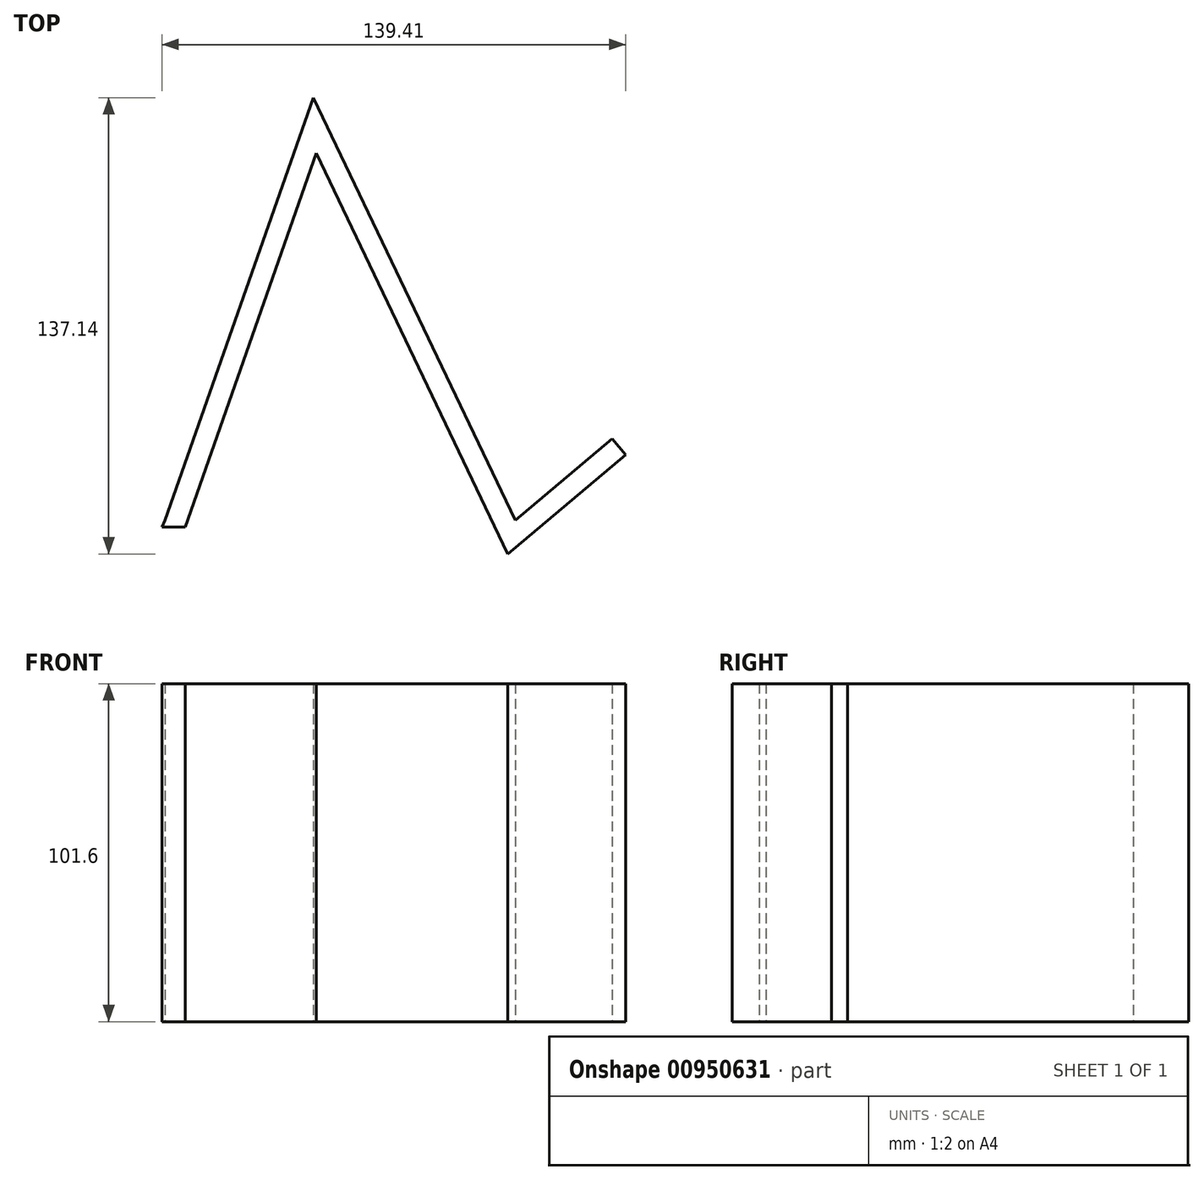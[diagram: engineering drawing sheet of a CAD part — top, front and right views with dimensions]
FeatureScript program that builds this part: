
annotation { "Feature Type Name" : "Feature", "Feature Type Description" : "" }
export const myFeature = defineFeature(function(context is Context, id is Id, definition is map)
    precondition{}
    {
        {
            var Q0;
            Q0=qCreatedBy(makeId("Top.planeOp"),FACE);
            var sketch = newSketch(context, id + "F0", { "sketchPlane" : qUnion([Q0])});
            skLineSegment(sketch, "E0", {"start": v(0, 0) * mm, "end": v(-60.67, 127) * mm});
            skLineSegment(sketch, "E1", {"start": v(-60.67, 127) * mm, "end": v(-105.18, 0) * mm});
            skLineSegment(sketch, "E2", {"start": v(0, 0) * mm, "end": v(29.17, 24.51) * mm});
            skLineSegment(sketch, "E3.0", {"start": v(-59.77, 110.38) * mm, "end": v(-99.2, -2.1) * mm});
            skLineSegment(sketch, "E3.1", {"start": v(-2.2, -10.14) * mm, "end": v(-59.77, 110.38) * mm});
            skLineSegment(sketch, "E3.2", {"start": v(-2.2, -10.14) * mm, "end": v(33.25, 19.65) * mm});
            skLineSegment(sketch, "E4", {"start": v(-99.2, -2.1) * mm, "end": v(-106.16, -2.1) * mm});
            skLineSegment(sketch, "E5", {"start": v(-106.16, -2.1) * mm, "end": v(-105.18, 0) * mm});
            skLineSegment(sketch, "E6", {"start": v(29.17, 24.51) * mm, "end": v(33.25, 19.65) * mm});
            skSolve(sketch);
        }
        {
            var Q0;
            Q0 = qSketchRegion(id + "F0", true);
            extrude(context, id + "F1", {"entities" : qUnion([Q0]), "depth" : 101.6 * mm, "offsetDistance" : 25.4 * mm});
        }
    });
